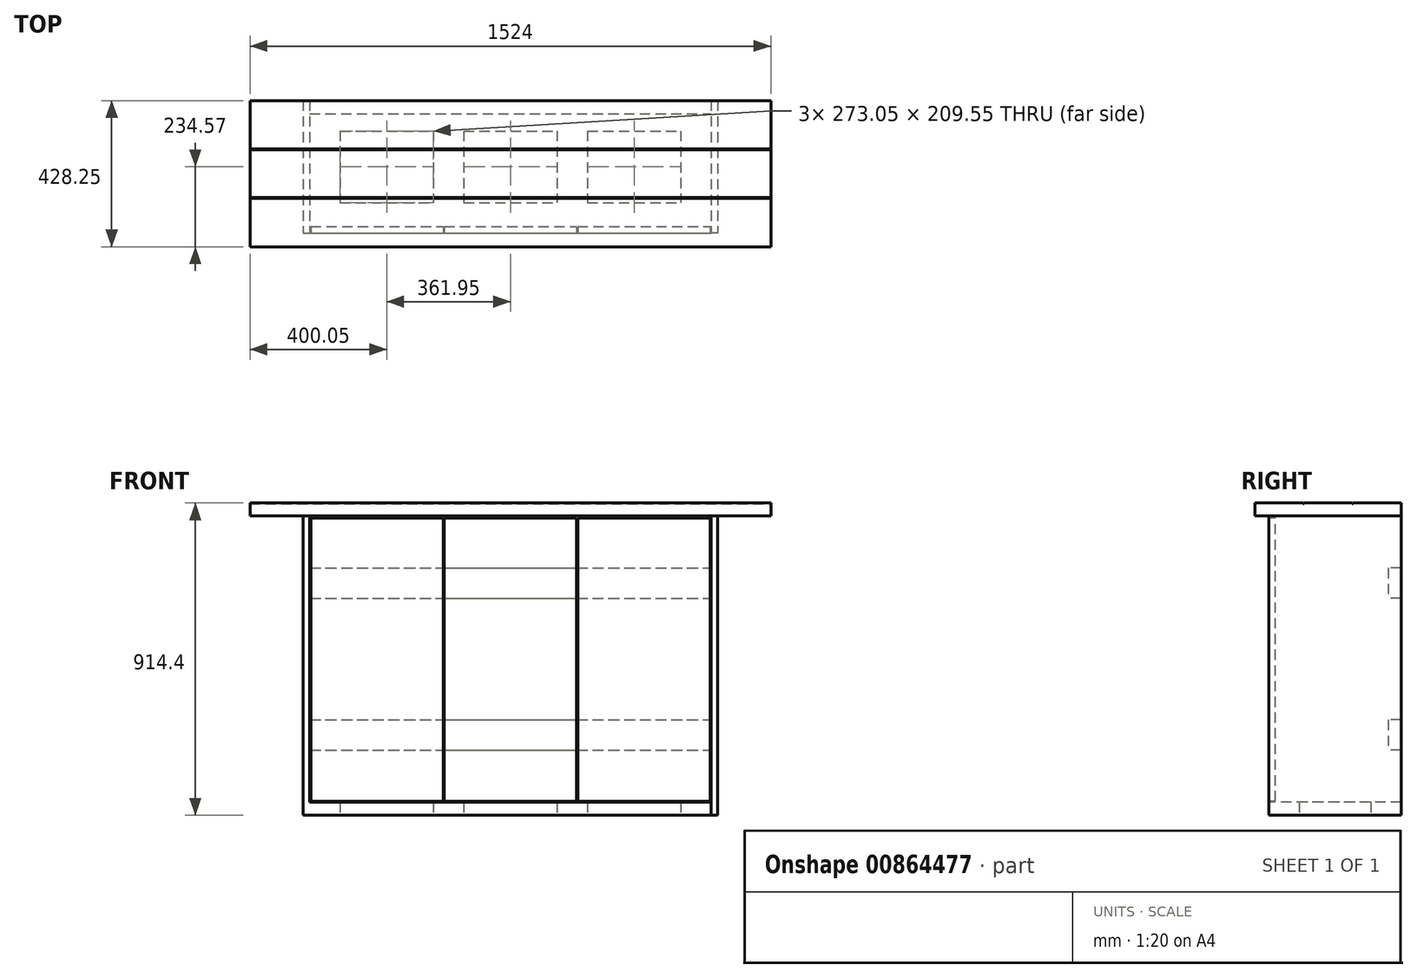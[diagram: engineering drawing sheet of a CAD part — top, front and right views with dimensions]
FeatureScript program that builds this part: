
annotation { "Feature Type Name" : "Feature", "Feature Type Description" : "" }
export const myFeature = defineFeature(function(context is Context, id is Id, definition is map)
    precondition{}
    {
        {
            var Q0;
            Q0=qCreatedBy(makeId("Top.planeOp"),FACE);
            var sketch = newSketch(context, id + "F0", { "sketchPlane" : qUnion([Q0])});
            skLineSegment(sketch, "E0.bottom", {"start": v(587.38, 193.68) * mm, "end": v(-587.38, 193.68) * mm, "construction": true});
            skLineSegment(sketch, "E0.top", {"start": v(587.38, -193.67) * mm, "end": v(-587.38, -193.68) * mm, "construction": true});
            skLineSegment(sketch, "E0.left", {"start": v(587.38, 193.68) * mm, "end": v(587.38, -193.67) * mm, "construction": true});
            skLineSegment(sketch, "E0.right", {"start": v(-587.38, 193.67) * mm, "end": v(-587.38, -193.68) * mm, "construction": true});
            skPoint(sketch, "E0.middle", {"position": v(0, 0) * mm});
            skLineSegment(sketch, "E1.bottom", {"start": v(-587.38, 193.68) * mm, "end": v(587.38, 193.68) * mm});
            skLineSegment(sketch, "E1.top", {"start": v(-587.38, 104.77) * mm, "end": v(587.38, 104.78) * mm});
            skLineSegment(sketch, "E1.left", {"start": v(-587.38, 193.67) * mm, "end": v(-587.38, 104.77) * mm});
            skLineSegment(sketch, "E1.right", {"start": v(587.38, 193.68) * mm, "end": v(587.38, 104.78) * mm});
            skLineSegment(sketch, "E2.bottom", {"start": v(-587.38, -193.68) * mm, "end": v(587.38, -193.67) * mm});
            skLineSegment(sketch, "E2.top", {"start": v(-587.38, -104.77) * mm, "end": v(587.38, -104.78) * mm});
            skLineSegment(sketch, "E2.left", {"start": v(-587.38, -193.68) * mm, "end": v(-587.38, -104.77) * mm});
            skLineSegment(sketch, "E2.right", {"start": v(587.38, -193.67) * mm, "end": v(587.38, -104.78) * mm});
            skLineSegment(sketch, "E3.bottom", {"start": v(-587.38, 104.77) * mm, "end": v(-498.48, 104.77) * mm});
            skLineSegment(sketch, "E3.top", {"start": v(-587.38, -104.77) * mm, "end": v(-498.48, -104.77) * mm});
            skLineSegment(sketch, "E3.left", {"start": v(-587.38, 104.77) * mm, "end": v(-587.38, -104.77) * mm});
            skLineSegment(sketch, "E3.right", {"start": v(-498.48, 104.77) * mm, "end": v(-498.48, -104.77) * mm});
            skLineSegment(sketch, "E4.bottom", {"start": v(-225.43, 104.78) * mm, "end": v(-136.53, 104.78) * mm});
            skLineSegment(sketch, "E4.top", {"start": v(-225.43, -104.77) * mm, "end": v(-136.53, -104.77) * mm});
            skLineSegment(sketch, "E4.left", {"start": v(-225.43, 104.78) * mm, "end": v(-225.43, -104.77) * mm});
            skLineSegment(sketch, "E4.right", {"start": v(-136.53, 104.78) * mm, "end": v(-136.53, -104.77) * mm});
            skLineSegment(sketch, "E5.bottom", {"start": v(136.52, 104.78) * mm, "end": v(225.42, 104.78) * mm});
            skLineSegment(sketch, "E5.top", {"start": v(136.52, -104.77) * mm, "end": v(225.42, -104.77) * mm});
            skLineSegment(sketch, "E5.left", {"start": v(136.52, 104.78) * mm, "end": v(136.52, -104.77) * mm});
            skLineSegment(sketch, "E5.right", {"start": v(225.42, 104.78) * mm, "end": v(225.42, -104.77) * mm});
            skLineSegment(sketch, "E6.bottom", {"start": v(587.38, 104.78) * mm, "end": v(498.48, 104.78) * mm});
            skLineSegment(sketch, "E6.top", {"start": v(587.38, -104.78) * mm, "end": v(498.48, -104.78) * mm});
            skLineSegment(sketch, "E6.left", {"start": v(587.38, 104.78) * mm, "end": v(587.38, -104.78) * mm});
            skLineSegment(sketch, "E6.right", {"start": v(498.48, 104.78) * mm, "end": v(498.48, -104.78) * mm});
            skSolve(sketch);
        }
        {
            var Q0;
            {var subQ13=sQuery(id+"F0.wireOp",EDGE,"E3.left");var subQ16=sQuery(id+"F0.wireOp",EDGE,"E6.left");Q0=qUnion([makeQuery(id+"F0.imprint","IMPRINT",FACE,{"disambiguationData":[TD([[makeQuery(id+"F0.imprint","IMPRINT",EDGE,{"derivedFrom":subQ16}),-1.0]])]}),makeQuery(id+"F0.imprint","IMPRINT",FACE,{"disambiguationData":[TD([[makeQuery(id+"F0.imprint","IMPRINT",EDGE,{"derivedFrom":sQuery(id+"F0.wireOp",EDGE,"E1.bottom")}),-1.0]])]}),makeQuery(id+"F0.imprint","IMPRINT",FACE,{"disambiguationData":[TD([[makeQuery(id+"F0.imprint","IMPRINT",EDGE,{"derivedFrom":subQ13}),1.0]])]}),makeQuery(id+"F0.imprint","IMPRINT",FACE,{"disambiguationData":[TD([[makeQuery(id+"F0.imprint","IMPRINT",EDGE,{"derivedFrom":sQuery(id+"F0.wireOp",EDGE,"E2.bottom")}),1.0]])]})]);}
            var Q1;
            {var subQ2=sQuery(id+"F0.wireOp",EDGE,"E5.left");Q1=makeQuery(id+"F0.imprint","IMPRINT",FACE,{"disambiguationData":[TD([[makeQuery(id+"F0.imprint","IMPRINT",EDGE,{"derivedFrom":subQ2}),1.0]])]});}
            var Q2;
            {var subQ2=sQuery(id+"F0.wireOp",EDGE,"E4.left");Q2=makeQuery(id+"F0.imprint","IMPRINT",FACE,{"disambiguationData":[TD([[makeQuery(id+"F0.imprint","IMPRINT",EDGE,{"derivedFrom":subQ2}),1.0]])]});}
            extrude(context, id + "F1", {"entities" : qUnion([Q0, Q1, Q2]), "depth" : 38.1 * mm, "offsetDistance" : 25.4 * mm});
        }
        {
            var Q0;
            Q0=makeQuery(id+"F1.opExtrude","SWEPT_FACE",FACE,{"disambiguationData":[OSD([sQuery(id+"F0.wireOp",EDGE,"E1.right"),sQuery(id+"F0.wireOp",EDGE,"E2.right"),sQuery(id+"F0.wireOp",EDGE,"E6.left")])]});
            var sketch = newSketch(context, id + "F2", { "sketchPlane" : qUnion([Q0])});
            skLineSegment(sketch, "E7.bottom", {"start": v(-193.68, 0) * mm, "end": v(193.68, 0) * mm});
            skLineSegment(sketch, "E7.top", {"start": v(-193.68, 876.3) * mm, "end": v(193.67, 876.3) * mm});
            skLineSegment(sketch, "E7.left", {"start": v(-193.68, 0) * mm, "end": v(-193.68, 876.3) * mm});
            skLineSegment(sketch, "E7.right", {"start": v(193.68, 0) * mm, "end": v(193.67, 876.3) * mm});
            skSolve(sketch);
        }
        {
            var Q0;
            {var subQ0=sQuery(id+"F2.wireOp",EDGE,"E7.top");Q0=makeQuery(id+"F2.imprint","IMPRINT",FACE,{"disambiguationData":[TD([[makeQuery(id+"F2.imprint","IMPRINT",EDGE,{"derivedFrom":subQ0}),-1.0]])]});}
            var Q1;
            {var subQ0=sQuery(id+"F2.wireOp",EDGE,"E7.bottom");Q1=makeQuery(id+"F2.imprint","IMPRINT",FACE,{"disambiguationData":[TD([[makeQuery(id+"F2.imprint","IMPRINT",EDGE,{"derivedFrom":subQ0}),-1.0]])]});}
            extrude(context, id + "F3", {"entities" : qUnion([Q0, Q1]), "depth" : 19.05 * mm, "offsetDistance" : 25.4 * mm});
        }
        {
            var Q0;
            Q0=makeQuery(id+"F1.opExtrude","SWEPT_FACE",FACE,{"disambiguationData":[OSD([sQuery(id+"F0.wireOp",EDGE,"E1.left"),sQuery(id+"F0.wireOp",EDGE,"E2.left"),sQuery(id+"F0.wireOp",EDGE,"E3.left")])]});
            var sketch = newSketch(context, id + "F4", { "sketchPlane" : qUnion([Q0])});
            skLineSegment(sketch, "E8.bottom", {"start": v(-193.68, 0) * mm, "end": v(193.68, 0) * mm});
            skLineSegment(sketch, "E8.top", {"start": v(-193.68, 876.3) * mm, "end": v(193.68, 876.3) * mm});
            skLineSegment(sketch, "E8.left", {"start": v(-193.68, 0) * mm, "end": v(-193.68, 876.3) * mm});
            skLineSegment(sketch, "E8.right", {"start": v(193.68, 0) * mm, "end": v(193.68, 876.3) * mm});
            skSolve(sketch);
        }
        {
            var Q0;
            {var subQ0=sQuery(id+"F4.wireOp",EDGE,"E8.top");Q0=makeQuery(id+"F4.imprint","IMPRINT",FACE,{"disambiguationData":[TD([[makeQuery(id+"F4.imprint","IMPRINT",EDGE,{"derivedFrom":subQ0}),-1.0]])]});}
            var Q1;
            {var subQ0=sQuery(id+"F4.wireOp",EDGE,"E8.bottom");Q1=makeQuery(id+"F4.imprint","IMPRINT",FACE,{"disambiguationData":[TD([[makeQuery(id+"F4.imprint","IMPRINT",EDGE,{"derivedFrom":subQ0}),1.0]])]});}
            extrude(context, id + "F5", {"entities" : qUnion([Q0, Q1]), "operationType" : NewBodyOperationType.ADD, "depth" : 19.05 * mm, "offsetDistance" : 25.4 * mm});
        }
        {
            var Q0;
            Q0=makeQuery(id+"F5.opExtrude","SWEPT_FACE",FACE,{"disambiguationData":[OSD([sQuery(id+"F4.wireOp",EDGE,"E8.top")])]});
            var sketch = newSketch(context, id + "F6", { "sketchPlane" : qUnion([Q0])});
            skLineSegment(sketch, "E9.bottom", {"start": v(-762, 193.68) * mm, "end": v(762, 193.68) * mm});
            skLineSegment(sketch, "E9.top", {"start": v(-762, -234.57) * mm, "end": v(762, -234.57) * mm});
            skLineSegment(sketch, "E9.left", {"start": v(-762, 193.68) * mm, "end": v(-762, -234.57) * mm});
            skLineSegment(sketch, "E9.right", {"start": v(762, 193.68) * mm, "end": v(762, -234.57) * mm});
            skPoint(sketch, "E10.endSnap0", {"position": v(0, -104.78) * mm});
            skLineSegment(sketch, "E11", {"start": v(0, -193.67) * mm, "end": v(0, 193.68) * mm, "construction": true});
            skSolve(sketch);
        }
        {
            var Q0;
            Q0 = qSketchRegion(id + "F6", true);
            extrude(context, id + "F7", {"entities" : qUnion([Q0]), "depth" : 38.1 * mm, "offsetDistance" : 25.4 * mm});
        }
        {
            var Q0;
            Q0=makeQuery(id+"F5.boolean.opBoolean","MERGE",FACE,{"derivedFrom":[makeQuery(id+"F1.opExtrude","SWEPT_FACE",FACE,{"disambiguationData":[OSD([sQuery(id+"F0.wireOp",EDGE,"E2.bottom")])]}),makeQuery(id+"F5.opExtrude","SWEPT_FACE",FACE,{"disambiguationData":[OSD([sQuery(id+"F4.wireOp",EDGE,"E8.right")])]})]});
            var sketch = newSketch(context, id + "F8", { "sketchPlane" : qUnion([Q0])});
            skLineSegment(sketch, "E12.0", {"start": v(-584.2, 41.28) * mm, "end": v(-584.2, 876.3) * mm, "construction": true});
            skLineSegment(sketch, "E13.0", {"start": v(-584.2, 41.27) * mm, "end": v(584.2, 41.27) * mm});
            skLineSegment(sketch, "E14.0", {"start": v(584.2, 41.28) * mm, "end": v(584.2, 876.3) * mm, "construction": true});
            skLineSegment(sketch, "E15", {"start": v(-584.2, 876.3) * mm, "end": v(584.2, 876.3) * mm, "construction": true});
            skLineSegment(sketch, "E16.0", {"start": v(-584.2, 869.95) * mm, "end": v(584.2, 869.95) * mm, "construction": true});
            skLineSegment(sketch, "E17.bottom", {"start": v(-584.2, 41.28) * mm, "end": v(-196.85, 41.28) * mm});
            skLineSegment(sketch, "E17.top", {"start": v(-584.2, 869.95) * mm, "end": v(-196.85, 869.95) * mm});
            skLineSegment(sketch, "E17.left", {"start": v(-584.2, 41.28) * mm, "end": v(-584.2, 869.95) * mm});
            skLineSegment(sketch, "E17.right", {"start": v(-196.85, 41.28) * mm, "end": v(-196.85, 869.95) * mm});
            skLineSegment(sketch, "E18.bottom", {"start": v(-193.68, 41.27) * mm, "end": v(193.68, 41.27) * mm});
            skLineSegment(sketch, "E18.top", {"start": v(-193.68, 869.95) * mm, "end": v(193.68, 869.95) * mm});
            skLineSegment(sketch, "E18.left", {"start": v(-193.68, 41.28) * mm, "end": v(-193.68, 869.95) * mm});
            skLineSegment(sketch, "E18.right", {"start": v(193.68, 41.28) * mm, "end": v(193.68, 869.95) * mm});
            skLineSegment(sketch, "E19.bottom", {"start": v(584.2, 41.27) * mm, "end": v(196.85, 41.27) * mm});
            skLineSegment(sketch, "E19.top", {"start": v(584.2, 869.95) * mm, "end": v(196.85, 869.95) * mm});
            skLineSegment(sketch, "E19.left", {"start": v(584.2, 41.28) * mm, "end": v(584.2, 869.95) * mm});
            skLineSegment(sketch, "E19.right", {"start": v(196.85, 41.27) * mm, "end": v(196.85, 869.95) * mm});
            skSolve(sketch);
        }
        {
            var Q0;
            Q0 = qSketchRegion(id + "F8", true);
            extrude(context, id + "F9", {"entities" : qUnion([Q0]), "oppositeDirection" : true, "depth" : 19.05 * mm, "offsetDistance" : 25.4 * mm});
        }
        {
            var Q0;
            Q0=makeQuery(id+"F7.opExtrude","CAP_FACE",FACE,{"disambiguationData":[OSD([sQuery(id+"F6.wireOp",EDGE,"E9.bottom"),sQuery(id+"F6.wireOp",EDGE,"E9.top"),sQuery(id+"F6.wireOp",EDGE,"E9.left"),sQuery(id+"F6.wireOp",EDGE,"E9.right")])],"isStart":false});
            var sketch = newSketch(context, id + "F10", { "sketchPlane" : qUnion([Q0])});
            skLineSegment(sketch, "E20.bottom", {"start": v(-762, 52.2) * mm, "end": v(762, 52.2) * mm});
            skLineSegment(sketch, "E20.top", {"start": v(-762, 49.66) * mm, "end": v(762, 49.66) * mm});
            skLineSegment(sketch, "E20.left", {"start": v(-762, 52.2) * mm, "end": v(-762, 49.66) * mm});
            skLineSegment(sketch, "E20.right", {"start": v(762, 52.2) * mm, "end": v(762, 49.66) * mm});
            skLineSegment(sketch, "E21", {"start": v(-762, 50.93) * mm, "end": v(762, 50.93) * mm, "construction": true});
            skLineSegment(sketch, "E22.0.1.0", {"start": v(-762, -90.55) * mm, "end": v(762, -90.55) * mm});
            skLineSegment(sketch, "E22.0.1.1", {"start": v(-762, -93.1) * mm, "end": v(762, -93.1) * mm});
            skLineSegment(sketch, "E22.0.1.2", {"start": v(762, -90.55) * mm, "end": v(762, -93.1) * mm});
            skLineSegment(sketch, "E22.0.1.3", {"start": v(-762, -90.55) * mm, "end": v(-762, -93.1) * mm});
            skLineSegment(sketch, "E22.direction1", {"start": v(-762, 52.2) * mm, "end": v(-787.4, 52.2) * mm, "construction": true});
            skLineSegment(sketch, "E22.direction2", {"start": v(-762, 52.2) * mm, "end": v(-762, -90.55) * mm, "construction": true});
            skSolve(sketch);
        }
        {
            var Q0;
            Q0 = qSketchRegion(id + "F10", true);
            extrude(context, id + "F11", {"entities" : qUnion([Q0]), "operationType" : NewBodyOperationType.REMOVE, "oppositeDirection" : true, "depth" : 2.54 * mm, "offsetDistance" : 25.4 * mm});
        }
        {
            var Q0;
            Q0=makeQuery(id+"F3.opExtrude","CAP_FACE",FACE,{"disambiguationData":[OSD([sQuery(id+"F2.wireOp",EDGE,"E7.bottom"),sQuery(id+"F2.wireOp",EDGE,"E7.top"),sQuery(id+"F2.wireOp",EDGE,"E7.left"),sQuery(id+"F2.wireOp",EDGE,"E7.right")])],"isStart":true});
            var sketch = newSketch(context, id + "F12", { "sketchPlane" : qUnion([Q0])});
            skLineSegment(sketch, "E23.bottom", {"start": v(-193.68, 279.4) * mm, "end": v(-155.58, 279.4) * mm});
            skLineSegment(sketch, "E23.top", {"start": v(-193.68, 190.5) * mm, "end": v(-155.58, 190.5) * mm});
            skLineSegment(sketch, "E23.left", {"start": v(-193.68, 279.4) * mm, "end": v(-193.68, 190.5) * mm});
            skLineSegment(sketch, "E23.right", {"start": v(-155.58, 279.4) * mm, "end": v(-155.58, 190.5) * mm});
            skLineSegment(sketch, "E24.bottom", {"start": v(-193.67, 723.9) * mm, "end": v(-155.57, 723.9) * mm});
            skLineSegment(sketch, "E24.top", {"start": v(-193.67, 635) * mm, "end": v(-155.57, 635) * mm});
            skLineSegment(sketch, "E24.left", {"start": v(-193.67, 723.9) * mm, "end": v(-193.67, 635) * mm});
            skLineSegment(sketch, "E24.right", {"start": v(-155.57, 723.9) * mm, "end": v(-155.57, 635) * mm});
            skSolve(sketch);
        }
        {
            var Q0;
            Q0 = qSketchRegion(id + "F12", true);
            extrude(context, id + "F13", {"entities" : qUnion([Q0]), "endBound" : BoundingType.UP_TO_NEXT, "depth" : 25.4 * mm, "offsetDistance" : 25.4 * mm});
        }
    });
